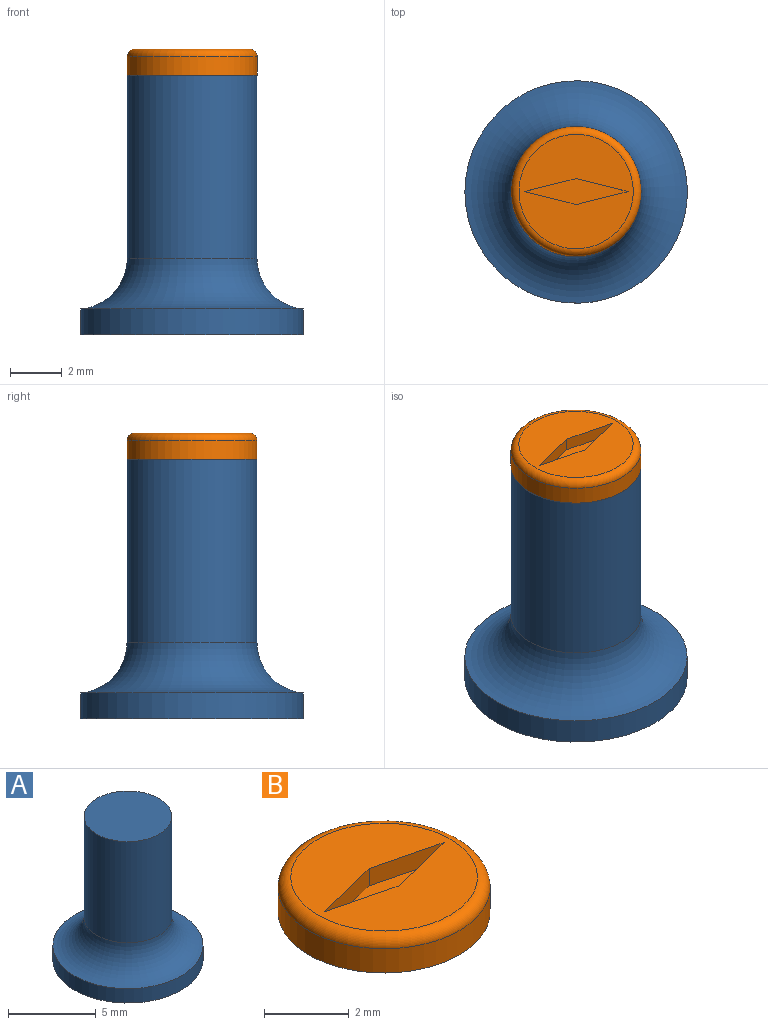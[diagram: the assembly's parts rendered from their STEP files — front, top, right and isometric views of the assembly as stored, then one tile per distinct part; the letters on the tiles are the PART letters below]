
ASSEMBLY  parts=2 mates=1
PART A: 5 faces, bbox 9.6x9.6x10 mm
  f0: torus R=4.45mm, axis (0,0,-1), area 57.1mm2, adj f1,f4
  f1: cylinder r=2.5mm len=7.05mm, axis (0,0,-1), area 110.8mm2, adj f0,f2
  f2: plane 5x5mm, normal (0,0,1), area 19.6mm2, adj f1
  f3: plane 8.56x8.56mm, normal (0,0,-1), area 57.5mm2, adj f4
  f4: cylinder r=4.28mm len=8.56mm, axis (0,0,-1), area 26.9mm2, adj f0,f3
PART B: 9 faces, bbox 5.4x5.4x1 mm
  f0: plane 4.4x4.4mm, normal (0,0,1), area 13.2mm2, adj f3,f4,f5,f6,f7
  f1: plane 5x5mm, normal (0,0,-1), area 19.6mm2, adj f2
  f2: cylinder r=2.5mm len=5mm, axis (0,0,1), area 11mm2, adj f1,f3
  f3: torus R=2.2mm, axis (0,0,1), area 7.1mm2, adj f0,f2
  f4: plane 2x0.5mm, normal (0.24,-0.97,0), area 1mm2, adj f0,f5,f7,f8
  f5: plane 2x0.5mm, normal (0.24,0.97,0), area 1mm2, adj f0,f4,f6,f8
  f6: plane 2x0.5mm, normal (-0.24,0.97,0), area 1mm2, adj f0,f5,f7,f8
  f7: plane 2x0.5mm, normal (-0.24,-0.97,0), area 1mm2, adj f0,f4,f6,f8
  f8: plane 4x1mm, normal (0,0,1), area 2mm2, adj f4,f5,f6,f7
PLACE A at identity fixed
PLACE B t=(0,0,10)mm
MATE fastened B.f2 <-> A.f0  axis (0,0,-1) through (0,0,9)mm
